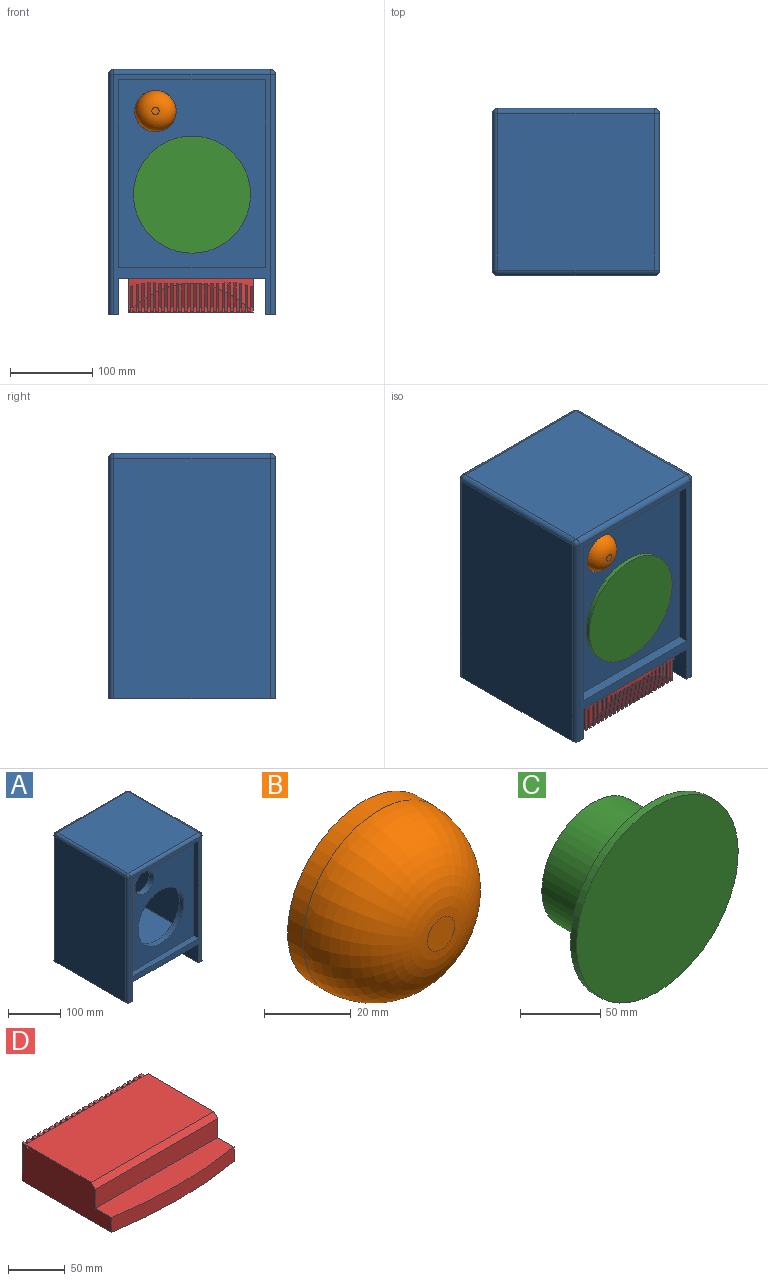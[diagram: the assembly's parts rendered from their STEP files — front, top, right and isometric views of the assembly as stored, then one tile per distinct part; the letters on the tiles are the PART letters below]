
ASSEMBLY  parts=4 mates=4
PART A: 36 faces, bbox 203.2x203.2x298.5 mm
  f0: plane 203.2x177.8mm, normal (0,0,-1), area 31592.5mm2, adj f1,f3,f19,f21,f23
  f1: plane 292.1x190.5mm, normal (0,-1,0), area 7096.8mm2, adj f0,f6,f7,f8,f9,f19,f20,f21
  f2: plane 292.1x190.5mm, normal (1,0,0), area 55645.1mm2, adj f22,f29,f33,f35
  f3: plane 292.1x190.5mm, normal (0,1,0), area 47741.8mm2, adj f0,f19,f20,f21,f22,f24,f28,f29
  f4: plane 292.1x190.5mm, normal (-1,0,0), area 55645.1mm2, adj f20,f24,f26,f27
  f5: plane 190.5x190.5mm, normal (0,0,1), area 36290.2mm2, adj f27,f28,f32,f33
  f6: plane 228.6x12.7mm, normal (-1,0,0), area 2903.2mm2, adj f1,f8,f9,f13
  f7: plane 228.6x12.7mm, normal (1,0,0), area 2903.2mm2, adj f1,f8,f9,f13
  f8: plane 177.8x12.7mm, normal (0,0,-1), area 2258.1mm2, adj f1,f6,f7,f13
  f9: plane 177.8x12.7mm, normal (0,0,1), area 2258.1mm2, adj f1,f6,f7,f13
  f10: cylinder r=61.98mm len=123.95mm, axis (0,-1,0), area 4945.5mm2, adj f12,f13
  f11: cylinder r=25.4mm len=50.8mm, axis (0,-1,0), area 2026.8mm2, adj f12,f13
  f12: plane 228.6x177.8mm, normal (0,1,0), area 26551.3mm2, adj f10,f11,f15,f16,f17,f18
  f13: plane 228.6x177.8mm, normal (0,-1,0), area 26551.3mm2, adj f6,f7,f8,f9,f10,f11
  f14: plane 228.6x177.8mm, normal (0,-1,0), area 40645.1mm2, adj f15,f16,f17,f18
  f15: plane 177.8x165.1mm, normal (0,0,-1), area 29354.8mm2, adj f12,f14,f17,f18
  f16: plane 177.8x165.1mm, normal (0,0,1), area 24818.3mm2, adj f12,f14,f17,f18,f23
  f17: plane 228.6x165.1mm, normal (1,0,0), area 37741.9mm2, adj f12,f14,f15,f16
  f18: plane 228.6x165.1mm, normal (-1,0,0), area 37741.9mm2, adj f12,f14,f15,f16
  f19: plane 203.2x44.45mm, normal (1,0,0), area 9032.2mm2, adj f0,f1,f3,f20
  f20: plane 203.2x12.7mm, normal (0,0,-1), area 2563.3mm2, adj f1,f3,f4,f19,f24,f26
  f21: plane 203.2x44.45mm, normal (-1,0,0), area 9032.2mm2, adj f0,f1,f3,f22
  f22: plane 203.2x12.7mm, normal (0,0,-1), area 2563.3mm2, adj f1,f2,f3,f21,f29,f35
  f23: cylinder r=38mm len=76mm, axis (0,0,-1), area 3032.3mm2, adj f0,f16
  f24: cylinder r=6.35mm len=292.1mm, axis (0,0,1), area 2913.6mm2, adj f3,f4,f20,f25
  f25: sphere r=6.35mm, area 63.3mm2, adj f24,f27,f28
  f26: cylinder r=6.35mm len=292.1mm, axis (0,0,-1), area 2913.6mm2, adj f1,f4,f20,f30
  f27: cylinder r=6.35mm len=190.5mm, axis (0,1,0), area 1900.2mm2, adj f4,f5,f25,f30
  f28: cylinder r=6.35mm len=190.5mm, axis (1,0,0), area 1900.2mm2, adj f3,f5,f25,f31
  f29: cylinder r=6.35mm len=292.1mm, axis (0,0,-1), area 2913.6mm2, adj f2,f3,f22,f31
  f30: sphere r=6.35mm, area 63.3mm2, adj f26,f27,f32
  f31: sphere r=6.35mm, area 63.3mm2, adj f28,f29,f33
  f32: cylinder r=6.35mm len=190.5mm, axis (-1,0,0), area 1900.2mm2, adj f1,f5,f30,f34
  f33: cylinder r=6.35mm len=190.5mm, axis (0,-1,0), area 1900.2mm2, adj f2,f5,f31,f34
  f34: sphere r=6.35mm, area 63.3mm2, adj f32,f33,f35
  f35: cylinder r=6.35mm len=292.1mm, axis (0,0,1), area 2913.6mm2, adj f1,f2,f22,f34
PART B: 4 faces, bbox 49.5x25.4x49.5 mm
  f0: cylinder r=24.77mm len=49.53mm, axis (0,1,0), area 790.5mm2, adj f2,f3
  f1: plane 8.89x8.89mm, normal (0,-1,0), area 62.1mm2, adj f3
  f2: plane 49.53x49.53mm, normal (0,1,0), area 1926.8mm2, adj f0
  f3: torus R=4.45mm, axis (0,-1,0), area 3485.8mm2, adj f0,f1
PART C: 5 faces, bbox 142.5x56.9x142.5 mm
  f0: cylinder r=71.25mm len=142.49mm, axis (0,1,0), area 2387.8mm2, adj f1,f2
  f1: plane 142.49x142.49mm, normal (0,-1,0), area 15947.1mm2, adj f0
  f2: plane 142.49x142.49mm, normal (0,1,0), area 9597.3mm2, adj f0,f3
  f3: cylinder r=44.96mm len=89.92mm, axis (0,-1,0), area 14565.2mm2, adj f2,f4
  f4: plane 89.92x89.92mm, normal (0,1,0), area 6349.9mm2, adj f3
PART D: 157 faces, bbox 152.4x123.8x41.3 mm
  f0: plane 111.13x41.28mm, normal (1,0,0), area 3834.5mm2, adj f85,f106,f107,f108,f109,f110,f112,f133
  f1: plane 32.55x15.88mm, normal (1,0,0), area 263.2mm2, adj f82,f84,f111,f154,f155
  f2: plane 31.73x15.4mm, normal (-1,0,0), area 251.3mm2, adj f83,f84,f111,f134,f155
  f3: plane 30.7x14.81mm, normal (1,0,0), area 235.1mm2, adj f83,f85,f112,f134,f155
  f4: plane 35.3x20.63mm, normal (1,0,0), area 325.6mm2, adj f6,f73,f97,f124,f145,f155
  f5: plane 35.3x20.59mm, normal (-1,0,0), area 325.6mm2, adj f6,f74,f97,f124,f146,f155
  f6: cylinder r=6.35mm len=3.18mm, axis (-1,0,0), area 10.5mm2, adj f4,f5,f124,f155
  f7: plane 35.3x20.53mm, normal (1,0,0), area 325.5mm2, adj f9,f74,f98,f125,f146,f155
  f8: plane 35.3x20.44mm, normal (-1,0,0), area 325.5mm2, adj f9,f75,f98,f125,f147,f155
  f9: cylinder r=6.35mm len=3.18mm, axis (-1,0,0), area 10.1mm2, adj f7,f8,f125,f155
  f10: plane 35.3x20.32mm, normal (1,0,0), area 325.3mm2, adj f12,f75,f99,f126,f147,f155
  f11: plane 35.3x20.19mm, normal (-1,0,0), area 325mm2, adj f12,f76,f99,f126,f148,f155
  f12: cylinder r=6.35mm len=3.18mm, axis (-1,0,0), area 9.3mm2, adj f10,f11,f126,f155
  f13: plane 35.3x20mm, normal (1,0,0), area 324.5mm2, adj f15,f76,f100,f127,f148,f155
  f14: plane 35.3x19.83mm, normal (-1,0,0), area 323.8mm2, adj f15,f77,f100,f127,f149,f155
  f15: cylinder r=6.35mm len=3.18mm, axis (-1,0,0), area 8.3mm2, adj f13,f14,f127,f155
  f16: plane 35.3x19.59mm, normal (1,0,0), area 322.5mm2, adj f18,f77,f101,f128,f149,f155
  f17: plane 35.3x19.36mm, normal (-1,0,0), area 321mm2, adj f18,f78,f101,f128,f150,f155
  f18: cylinder r=6.35mm len=3.18mm, axis (-1,0,0), area 6.8mm2, adj f16,f17,f128,f155
  f19: plane 35.3x19.06mm, normal (1,0,0), area 318.6mm2, adj f21,f78,f102,f129,f150,f155
  f20: plane 35.3x18.78mm, normal (-1,0,0), area 316mm2, adj f21,f79,f102,f129,f151,f155
  f21: cylinder r=6.35mm len=3.18mm, axis (-1,0,0), area 5mm2, adj f19,f20,f129,f155
  f22: plane 35.3x18.42mm, normal (1,0,0), area 311.8mm2, adj f24,f79,f103,f130,f151,f155
  f23: plane 35.3x18.1mm, normal (-1,0,0), area 307.4mm2, adj f24,f80,f103,f130,f152,f155
  f24: cylinder r=6.35mm len=3.18mm, axis (-1,0,0), area 2.8mm2, adj f22,f23,f130,f155
  f25: plane 35.3x17.68mm, normal (1,0,0), area 300.9mm2, adj f27,f80,f104,f131,f152,f155
  f26: plane 35.04x17.31mm, normal (-1,0,0), area 294.2mm2, adj f81,f104,f131,f153,f155
  f27: cylinder r=6.35mm len=1.91mm, axis (-1,0,0), area 0.2mm2, adj f25,f131,f155
  f28: plane 34.21x16.83mm, normal (1,0,0), area 284.7mm2, adj f81,f105,f132,f153,f155
  f29: plane 33.48x16.41mm, normal (-1,0,0), area 275.7mm2, adj f82,f105,f132,f154,f155
  f30: plane 111.13x41.28mm, normal (-1,0,0), area 4054.4mm2, adj f61,f106,f107,f108,f109,f110,f133,f155
  f31: plane 30.52x14.71mm, normal (1,0,0), area 232.2mm2, adj f61,f62,f86,f113,f155
  f32: plane 31.4x15.21mm, normal (-1,0,0), area 246.2mm2, adj f63,f86,f113,f135,f155
  f33: plane 32.39x15.78mm, normal (1,0,0), area 260.9mm2, adj f63,f87,f114,f135,f155
  f34: plane 33.18x16.24mm, normal (-1,0,0), area 271.7mm2, adj f64,f87,f114,f136,f155
  f35: plane 34.07x16.75mm, normal (1,0,0), area 283mm2, adj f64,f88,f115,f136,f155
  f36: plane 34.77x17.16mm, normal (-1,0,0), area 291.2mm2, adj f65,f88,f115,f137,f155
  f37: plane 35.3x17.61mm, normal (1,0,0), area 299.6mm2, adj f39,f65,f89,f116,f137,f155
  f38: plane 35.3x17.97mm, normal (-1,0,0), area 305.4mm2, adj f39,f66,f89,f116,f138,f155
  f39: cylinder r=6.35mm len=3.18mm, axis (-1,0,0), area 1.2mm2, adj f37,f38,f116,f155
  f40: plane 35.3x18.36mm, normal (1,0,0), area 311mm2, adj f42,f66,f90,f117,f138,f155
  f41: plane 35.3x18.67mm, normal (-1,0,0), area 314.7mm2, adj f42,f67,f90,f117,f139,f155
  f42: cylinder r=6.35mm len=3.18mm, axis (-1,0,0), area 3.7mm2, adj f40,f41,f117,f155
  f43: plane 35.3x19.01mm, normal (1,0,0), area 318.1mm2, adj f45,f67,f91,f118,f139,f155
  f44: plane 35.3x19.26mm, normal (-1,0,0), area 320.3mm2, adj f45,f68,f91,f118,f140,f155
  f45: cylinder r=6.35mm len=3.18mm, axis (-1,0,0), area 5.7mm2, adj f43,f44,f118,f155
  f46: plane 35.3x19.54mm, normal (1,0,0), area 322.2mm2, adj f48,f68,f92,f119,f140,f155
  f47: plane 35.3x19.75mm, normal (-1,0,0), area 323.4mm2, adj f48,f69,f92,f119,f141,f155
  f48: cylinder r=6.35mm len=3.18mm, axis (-1,0,0), area 7.4mm2, adj f46,f47,f119,f155
  f49: plane 35.3x19.97mm, normal (1,0,0), area 324.4mm2, adj f51,f69,f93,f120,f141,f155
  f50: plane 35.3x20.13mm, normal (-1,0,0), area 324.9mm2, adj f51,f70,f93,f120,f142,f155
  f51: cylinder r=6.35mm len=3.18mm, axis (-1,0,0), area 8.7mm2, adj f49,f50,f120,f155
  f52: plane 35.3x20.29mm, normal (1,0,0), area 325.3mm2, adj f54,f70,f94,f121,f142,f155
  f53: plane 35.3x20.41mm, normal (-1,0,0), area 325.4mm2, adj f54,f71,f94,f121,f143,f155
  f54: cylinder r=6.35mm len=3.18mm, axis (-1,0,0), area 9.6mm2, adj f52,f53,f121,f155
  f55: plane 35.3x20.51mm, normal (1,0,0), area 325.5mm2, adj f57,f71,f95,f122,f143,f155
  f56: plane 35.3x20.57mm, normal (-1,0,0), area 325.6mm2, adj f57,f72,f95,f122,f144,f155
  f57: cylinder r=6.35mm len=3.18mm, axis (-1,0,0), area 10.3mm2, adj f55,f56,f122,f155
  f58: plane 35.3x20.62mm, normal (1,0,0), area 325.6mm2, adj f60,f72,f96,f123,f144,f155
  f59: plane 35.3x20.64mm, normal (-1,0,0), area 325.6mm2, adj f60,f73,f96,f123,f145,f155
  f60: cylinder r=6.35mm len=3.18mm, axis (-1,0,0), area 10.5mm2, adj f58,f59,f123,f155
  f61: cylinder r=41.27mm len=12.95mm, axis (1,0,0), area 34.8mm2, adj f30,f31,f62,f133,f155
  f62: plane 2.02x1.83mm, normal (0,0.98,0.18), area 1.9mm2, adj f31,f61,f155
  f63: plane 7.75x3.81mm, normal (0,0.98,0.18), area 24mm2, adj f32,f33,f135,f155
  f64: plane 13.07x3.81mm, normal (0,0.98,0.18), area 45.2mm2, adj f34,f35,f136,f155
  f65: plane 17.8x3.81mm, normal (0,0.98,0.18), area 64.1mm2, adj f36,f37,f137,f155
  f66: plane 21.93x3.99mm, normal (0,0.98,0.18), area 80.8mm2, adj f38,f40,f138,f155
  f67: plane 25.47x4.63mm, normal (0,0.98,0.18), area 95.1mm2, adj f41,f43,f139,f155
  f68: plane 28.42x5.17mm, normal (0,0.98,0.18), area 107.1mm2, adj f44,f46,f140,f155
  f69: plane 30.78x5.6mm, normal (0,0.98,0.18), area 116.9mm2, adj f47,f49,f141,f155
  f70: plane 32.56x5.92mm, normal (0,0.98,0.18), area 124.4mm2, adj f50,f52,f142,f155
  f71: plane 33.75x6.14mm, normal (0,0.98,0.18), area 129.6mm2, adj f53,f55,f143,f155
  f72: plane 34.36x6.25mm, normal (0,0.98,0.18), area 132.6mm2, adj f56,f58,f144,f155
  f73: plane 34.45x6.26mm, normal (0,0.98,0.18), area 133.3mm2, adj f4,f59,f145,f155
  f74: plane 34.21x6.22mm, normal (0,0.98,0.18), area 131.8mm2, adj f5,f7,f146,f155
  f75: plane 33.38x6.07mm, normal (0,0.98,0.18), area 128mm2, adj f8,f10,f147,f155
  f76: plane 31.98x5.81mm, normal (0,0.98,0.18), area 121.9mm2, adj f11,f13,f148,f155
  f77: plane 29.99x5.45mm, normal (0,0.98,0.18), area 113.6mm2, adj f14,f16,f149,f155
  f78: plane 27.41x4.98mm, normal (0,0.98,0.18), area 103mm2, adj f17,f19,f150,f155
  f79: plane 24.25x4.41mm, normal (0,0.98,0.18), area 90.1mm2, adj f20,f22,f151,f155
  f80: plane 20.5x3.81mm, normal (0,0.98,0.18), area 75mm2, adj f23,f25,f152,f155
  f81: plane 16.15x3.81mm, normal (0,0.98,0.18), area 57.5mm2, adj f26,f28,f153,f155
  f82: plane 11.21x3.81mm, normal (0,0.98,0.18), area 37.8mm2, adj f1,f29,f154,f155
  f83: plane 5.67x3.81mm, normal (0,0.98,0.18), area 15.7mm2, adj f2,f3,f134,f155
  f84: cylinder r=41.27mm len=3.18mm, axis (-1,0,0), area 5.2mm2, adj f1,f2,f111,f133
  f85: cylinder r=41.27mm len=3.18mm, axis (-1,0,0), area 5.2mm2, adj f0,f3,f112,f133
  f86: cylinder r=41.27mm len=3.18mm, axis (-1,0,0), area 5.2mm2, adj f31,f32,f113,f133
  f87: cylinder r=41.27mm len=3.18mm, axis (-1,0,0), area 5.2mm2, adj f33,f34,f114,f133
  f88: cylinder r=41.27mm len=3.18mm, axis (-1,0,0), area 5.2mm2, adj f35,f36,f115,f133
  f89: cylinder r=41.27mm len=3.18mm, axis (-1,0,0), area 5.2mm2, adj f37,f38,f116,f133
  f90: cylinder r=41.27mm len=3.18mm, axis (-1,0,0), area 5.2mm2, adj f40,f41,f117,f133
  f91: cylinder r=41.27mm len=3.18mm, axis (-1,0,0), area 5.2mm2, adj f43,f44,f118,f133
  f92: cylinder r=41.27mm len=3.18mm, axis (-1,0,0), area 5.2mm2, adj f46,f47,f119,f133
  f93: cylinder r=41.27mm len=3.18mm, axis (-1,0,0), area 5.2mm2, adj f49,f50,f120,f133
  f94: cylinder r=41.27mm len=3.18mm, axis (-1,0,0), area 5.2mm2, adj f52,f53,f121,f133
  f95: cylinder r=41.27mm len=3.18mm, axis (-1,0,0), area 5.2mm2, adj f55,f56,f122,f133
  f96: cylinder r=41.27mm len=3.18mm, axis (-1,0,0), area 5.2mm2, adj f58,f59,f123,f133
  f97: cylinder r=41.27mm len=3.18mm, axis (-1,0,0), area 5.2mm2, adj f4,f5,f124,f133
  f98: cylinder r=41.27mm len=3.18mm, axis (-1,0,0), area 5.2mm2, adj f7,f8,f125,f133
  f99: cylinder r=41.27mm len=3.18mm, axis (-1,0,0), area 5.2mm2, adj f10,f11,f126,f133
  f100: cylinder r=41.27mm len=3.18mm, axis (-1,0,0), area 5.2mm2, adj f13,f14,f127,f133
  f101: cylinder r=41.27mm len=3.18mm, axis (-1,0,0), area 5.2mm2, adj f16,f17,f128,f133
  f102: cylinder r=41.27mm len=3.18mm, axis (-1,0,0), area 5.2mm2, adj f19,f20,f129,f133
  f103: cylinder r=41.27mm len=3.18mm, axis (-1,0,0), area 5.2mm2, adj f22,f23,f130,f133
  f104: cylinder r=41.27mm len=3.18mm, axis (-1,0,0), area 5.2mm2, adj f25,f26,f131,f133
  f105: cylinder r=41.27mm len=3.18mm, axis (-1,0,0), area 5.2mm2, adj f28,f29,f132,f133
  f106: plane 152.4x81.66mm, normal (0,0,1), area 12444.7mm2, adj f0,f30,f110,f133
  f107: plane 152.4x123.83mm, normal (0,0,-1), area 18227.6mm2, adj f0,f30,f155,f156
  f108: plane 152.4x20.32mm, normal (0,-1,0), area 3096.8mm2, adj f0,f30,f109,f110
  f109: plane 152.4x26.48mm, normal (0,0,1), area 3713.4mm2, adj f0,f30,f108,f156
  f110: plane 152.4x5.08mm, normal (0,-0.71,0.71), area 1094.9mm2, adj f0,f30,f106,f108
  f111: plane 27.5x15.88mm, normal (0,0.87,0.5), area 99.3mm2, adj f1,f2,f84,f155
  f112: plane 25.65x14.81mm, normal (0,0.87,0.5), area 92.4mm2, adj f0,f3,f85,f155
  f113: plane 26.34x15.21mm, normal (0,0.87,0.5), area 95mm2, adj f31,f32,f86,f155
  f114: plane 28.12x16.24mm, normal (0,0.87,0.5), area 101.7mm2, adj f33,f34,f87,f155
  f115: plane 29.71x17.16mm, normal (0,0.87,0.5), area 107.7mm2, adj f35,f36,f88,f155
  f116: plane 30.25x17.46mm, normal (0,0.87,0.5), area 110.9mm2, adj f37,f38,f39,f89
  f117: plane 30.25x17.46mm, normal (0,0.87,0.5), area 110.9mm2, adj f40,f41,f42,f90
  f118: plane 30.25x17.46mm, normal (0,0.87,0.5), area 110.9mm2, adj f43,f44,f45,f91
  f119: plane 30.25x17.46mm, normal (0,0.87,0.5), area 110.9mm2, adj f46,f47,f48,f92
  f120: plane 30.25x17.46mm, normal (0,0.87,0.5), area 110.9mm2, adj f49,f50,f51,f93
  f121: plane 30.25x17.46mm, normal (0,0.87,0.5), area 110.9mm2, adj f52,f53,f54,f94
  f122: plane 30.25x17.46mm, normal (0,0.87,0.5), area 110.9mm2, adj f55,f56,f57,f95
  f123: plane 30.25x17.46mm, normal (0,0.87,0.5), area 110.9mm2, adj f58,f59,f60,f96
  f124: plane 30.25x17.46mm, normal (0,0.87,0.5), area 110.9mm2, adj f4,f5,f6,f97
  f125: plane 30.25x17.46mm, normal (0,0.87,0.5), area 110.9mm2, adj f7,f8,f9,f98
  f126: plane 30.25x17.46mm, normal (0,0.87,0.5), area 110.9mm2, adj f10,f11,f12,f99
  f127: plane 30.25x17.46mm, normal (0,0.87,0.5), area 110.9mm2, adj f13,f14,f15,f100
  f128: plane 30.25x17.46mm, normal (0,0.87,0.5), area 110.9mm2, adj f16,f17,f18,f101
  f129: plane 30.25x17.46mm, normal (0,0.87,0.5), area 110.9mm2, adj f19,f20,f21,f102
  f130: plane 30.25x17.46mm, normal (0,0.87,0.5), area 110.9mm2, adj f22,f23,f24,f103
  f131: plane 30.25x17.46mm, normal (0,0.87,0.5), area 110.7mm2, adj f25,f26,f27,f104,f155
  f132: plane 29.16x16.83mm, normal (0,0.87,0.5), area 105.6mm2, adj f28,f29,f105,f155
  f133: plane 152.4x8.61mm, normal (0,0.48,-0.88), area 1498mm2, adj f0,f30,f61,f84,f85,f86,f87,f88
  f134: cylinder r=41.27mm len=12.95mm, axis (1,0,0), area 52.2mm2, adj f2,f3,f83,f133
  f135: cylinder r=41.27mm len=12.95mm, axis (1,0,0), area 52.2mm2, adj f32,f33,f63,f133
  f136: cylinder r=41.27mm len=12.95mm, axis (1,0,0), area 52.2mm2, adj f34,f35,f64,f133
  f137: cylinder r=41.27mm len=12.95mm, axis (1,0,0), area 52.2mm2, adj f36,f37,f65,f133
  f138: cylinder r=41.27mm len=12.95mm, axis (1,0,0), area 52.2mm2, adj f38,f40,f66,f133
  f139: cylinder r=41.27mm len=12.95mm, axis (1,0,0), area 52.2mm2, adj f41,f43,f67,f133
  f140: cylinder r=41.27mm len=12.95mm, axis (1,0,0), area 52.2mm2, adj f44,f46,f68,f133
  f141: cylinder r=41.27mm len=12.95mm, axis (1,0,0), area 52.2mm2, adj f47,f49,f69,f133
  f142: cylinder r=41.27mm len=12.95mm, axis (1,0,0), area 52.2mm2, adj f50,f52,f70,f133
  f143: cylinder r=41.27mm len=12.95mm, axis (1,0,0), area 52.2mm2, adj f53,f55,f71,f133
  f144: cylinder r=41.27mm len=12.95mm, axis (1,0,0), area 52.2mm2, adj f56,f58,f72,f133
  f145: cylinder r=41.27mm len=12.95mm, axis (1,0,0), area 52.2mm2, adj f4,f59,f73,f133
  f146: cylinder r=41.27mm len=12.95mm, axis (1,0,0), area 52.2mm2, adj f5,f7,f74,f133
  f147: cylinder r=41.27mm len=12.95mm, axis (1,0,0), area 52.2mm2, adj f8,f10,f75,f133
  f148: cylinder r=41.27mm len=12.95mm, axis (1,0,0), area 52.2mm2, adj f11,f13,f76,f133
  f149: cylinder r=41.27mm len=12.95mm, axis (1,0,0), area 52.2mm2, adj f14,f16,f77,f133
  f150: cylinder r=41.27mm len=12.95mm, axis (1,0,0), area 52.2mm2, adj f17,f19,f78,f133
  f151: cylinder r=41.27mm len=12.95mm, axis (1,0,0), area 52.2mm2, adj f20,f22,f79,f133
  f152: cylinder r=41.27mm len=12.95mm, axis (1,0,0), area 52.2mm2, adj f23,f25,f80,f133
  f153: cylinder r=41.27mm len=12.95mm, axis (1,0,0), area 52.2mm2, adj f26,f28,f81,f133
  f154: cylinder r=41.27mm len=12.95mm, axis (1,0,0), area 52.2mm2, adj f1,f29,f82,f133
  f155: cylinder r=460.38mm len=152.4mm, axis (0,0,-1), area 1955.3mm2, adj f0,f1,f2,f3,f4,f5,f6,f7
  f156: cylinder r=460.38mm len=152.4mm, axis (0,0,-1), area 2430.5mm2, adj f0,f30,f107,f109
PLACE A t=(-115.94,-126.38,-89.16)mm fixed
PLACE B t=(-1379.59,-202.58,132.34)mm
PLACE C t=(-552.15,-215.28,-31.42)mm
PLACE D rot(axis=(1,0,0),180deg) t=(-1005.74,-284.02,-89.16)mm
MATE revolute A.f10 <-> C.f0  axis (0,-1,0) through (-115.94,-215.28,12.44)mm
MATE planar D.f107 <-> A.f0  axis (0,0,1) through (-117.39,-165.14,-89.16)mm
MATE planar A.f13 <-> C.f0  axis (0,-1,0) through (-112.54,-215.28,43.57)mm
MATE fastened B.f0 <-> A.f11  axis (0,1,0) through (-160.39,-202.58,114.04)mm
